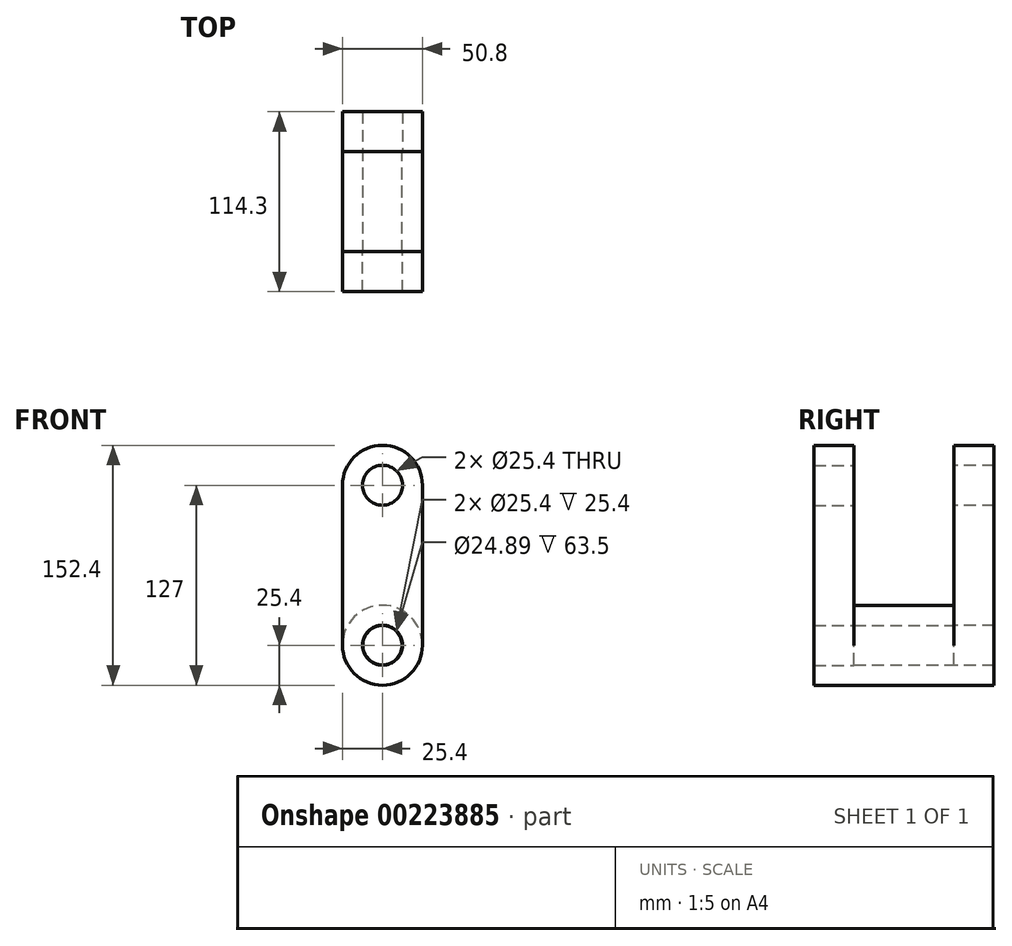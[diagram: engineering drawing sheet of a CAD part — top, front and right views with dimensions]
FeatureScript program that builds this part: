
annotation { "Feature Type Name" : "Feature", "Feature Type Description" : "" }
export const myFeature = defineFeature(function(context is Context, id is Id, definition is map)
    precondition{}
    {
        {
            var Q0;
            Q0=qCreatedBy(makeId("Front.planeOp"),FACE);
            var sketch = newSketch(context, id + "F0", { "sketchPlane" : qUnion([Q0])});
            skLineSegment(sketch, "E0.left", {"start": v(25.4, -50.8) * mm, "end": v(25.4, 50.8) * mm});
            skLineSegment(sketch, "E0.right", {"start": v(-25.4, -50.8) * mm, "end": v(-25.4, 50.8) * mm});
            skPoint(sketch, "E0.middle", {"position": v(0, 0) * mm});
            skArc(sketch, "E1", {"start": v(25.4, 50.8) * mm, "mid": v(0, 76.2) * mm, "end": v(-25.4, 50.8) * mm});
            skArc(sketch, "E2", {"start": v(-25.4, -50.8) * mm, "mid": v(0, -76.2) * mm, "end": v(25.4, -50.8) * mm});
            skCircle(sketch, "E3", {"center": v(0, 50.8) * mm, "radius": 12.7 * mm});
            skCircle(sketch, "E4", {"center": v(0, -50.8) * mm, "radius": 12.7 * mm});
            skSolve(sketch);
        }
        {
            var Q0;
            Q0 = qSketchRegion(id + "F0", true);
            extrude(context, id + "F1", {"entities" : qUnion([Q0]), "oppositeDirection" : true, "depth" : 25.4 * mm});
        }
        {
            var Q0;
            Q0=makeQuery(id+"F1.opExtrude","CAP_FACE",FACE,{"disambiguationData":[OSD([sQuery(id+"F0.wireOp",EDGE,"E0.left"),sQuery(id+"F0.wireOp",EDGE,"E0.right"),sQuery(id+"F0.wireOp",EDGE,"E1"),sQuery(id+"F0.wireOp",EDGE,"E2"),sQuery(id+"F0.wireOp",EDGE,"E3"),sQuery(id+"F0.wireOp",EDGE,"E4")])],"isStart":true});
            var sketch = newSketch(context, id + "F2", { "sketchPlane" : qUnion([Q0])});
            skCircle(sketch, "E5", {"center": v(0, -50.8) * mm, "radius": 12.45 * mm});
            skCircle(sketch, "E6", {"center": v(0, -50.8) * mm, "radius": 25.4 * mm});
            skSolve(sketch);
        }
        {
            var Q0;
            Q0 = qSketchRegion(id + "F2", true);
            extrude(context, id + "F3", {"entities" : qUnion([Q0]), "operationType" : NewBodyOperationType.ADD, "depth" : 63.5 * mm});
        }
        {
            var Q0;
            Q0=makeQuery(id+"F3.opExtrude","CAP_FACE",FACE,{"disambiguationData":[OSD([sQuery(id+"F2.wireOp",EDGE,"E5"),sQuery(id+"F2.wireOp",EDGE,"E6")])],"isStart":false});
            var sketch = newSketch(context, id + "F4", { "sketchPlane" : qUnion([Q0])});
            skCircle(sketch, "E7", {"center": v(0, -50.8) * mm, "radius": 12.7 * mm});
            skArc(sketch, "E8", {"start": v(-25.4, -50.8) * mm, "mid": v(0, -76.2) * mm, "end": v(25.4, -50.8) * mm});
            skLineSegment(sketch, "E9", {"start": v(25.4, -50.8) * mm, "end": v(25.4, 50.8) * mm});
            skLineSegment(sketch, "E10", {"start": v(-25.4, 50.8) * mm, "end": v(-25.4, -50.8) * mm});
            skArc(sketch, "E11", {"start": v(25.4, 50.8) * mm, "mid": v(0, 76.2) * mm, "end": v(-25.4, 50.8) * mm});
            skCircle(sketch, "E12", {"center": v(0, 50.8) * mm, "radius": 12.7 * mm});
            skSolve(sketch);
        }
        {
            var Q0;
            {var subQ1=sQuery(id+"F4.wireOp",EDGE,"E9");Q0=makeQuery(id+"F4.imprint","IMPRINT",FACE,{"disambiguationData":[TD([[makeQuery(id+"F4.imprint","IMPRINT",EDGE,{"derivedFrom":subQ1}),1.0]])]});}
            var Q1;
            Q1=makeQuery(id+"F4.imprint","IMPRINT",FACE,{"disambiguationData":[TD([[makeQuery(id+"F4.imprint","IMPRINT",EDGE,{"derivedFrom":sQuery(id+"F4.wireOp",EDGE,"E7")}),-1.0]])]});
            extrude(context, id + "F5", {"entities" : qUnion([Q0, Q1]), "operationType" : NewBodyOperationType.ADD, "depth" : 25.4 * mm});
        }
    });
